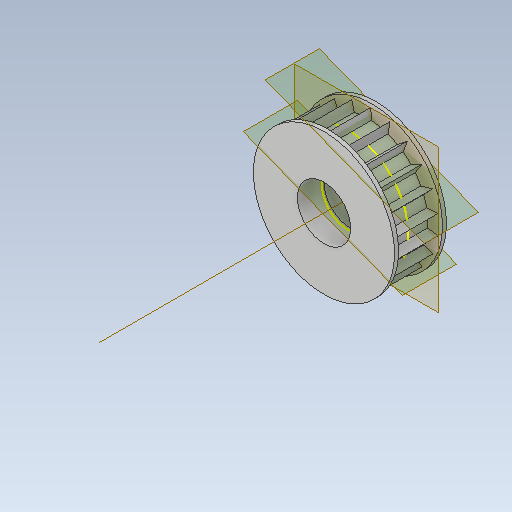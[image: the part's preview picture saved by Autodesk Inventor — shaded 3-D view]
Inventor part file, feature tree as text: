
AUTODESK INVENTOR PART (.ipt)
format: ipt  version: 2020 (Build 240168000, 168)  size: 418,816 bytes
history: native  units: mm
features: sketch x6, other x4, plane x4
ambient origin geometry x8: Origin, YZ Plane, XZ Plane, XY Plane, X Axis, Y Axis, Z Axis, Center Point
bodies: Solid1 (feature_tree)
feature tree (14):
  other  "rear-wheel.ipt"
  other  "Solid1::rear-wheel.ipt"
  other  "TaggingFeature1"
  sketch  "Sketch1"  dims[d0=10.0mm]
  sketch  "Sketch2"
  sketch  "Sketch3"
  sketch  "Sketch6"
  sketch  "Sketch7"
  sketch  "Sketch8"
  plane  "Work Plane1"
  plane  "Work Plane2"
  plane  "Work Plane3"
  plane  "Work Plane4"
  other  "Work Axis1"
